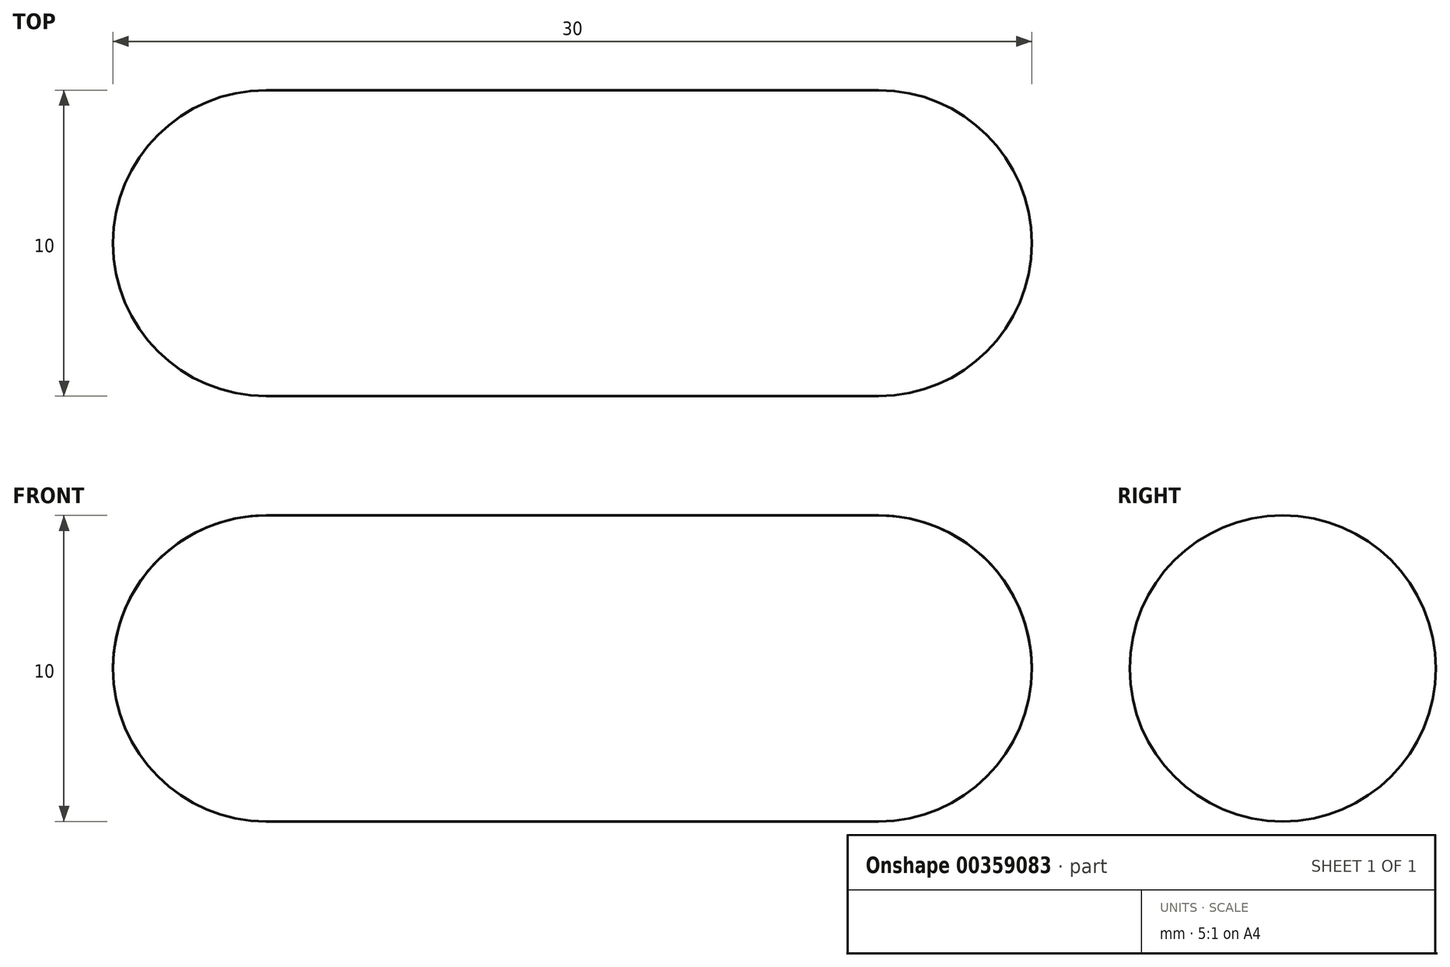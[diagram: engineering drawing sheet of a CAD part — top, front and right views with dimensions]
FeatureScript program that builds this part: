
annotation { "Feature Type Name" : "Feature", "Feature Type Description" : "" }
export const myFeature = defineFeature(function(context is Context, id is Id, definition is map)
    precondition{}
    {
        {
            var Q0;
            Q0=qCreatedBy(makeId("Top.planeOp"),FACE);
            var sketch = newSketch(context, id + "F0", { "sketchPlane" : qUnion([Q0])});
            skLineSegment(sketch, "E0.bottom", {"start": v(0, 0) * mm, "end": v(30, 0) * mm});
            skLineSegment(sketch, "E0.top", {"start": v(0, 10) * mm, "end": v(30, 10) * mm});
            skLineSegment(sketch, "E0.left", {"start": v(0, 0) * mm, "end": v(0, 10) * mm});
            skLineSegment(sketch, "E0.right", {"start": v(30, 0) * mm, "end": v(30, 10) * mm});
            skSolve(sketch);
        }
        {
            var Q0;
            Q0 = qSketchRegion(id + "F0", true);
            extrude(context, id + "F1", {"entities" : qUnion([Q0]), "depth" : 10 * mm});
        }
        {
            var Q0;
            Q0=makeQuery(id+"F1.opExtrude","CAP_EDGE",EDGE,{"disambiguationData":[OSD([sQuery(id+"F0.wireOp",EDGE,"E0.bottom")])],"isStart":false});
            var Q1;
            Q1=makeQuery(id+"F1.opExtrude","CAP_EDGE",EDGE,{"disambiguationData":[OSD([sQuery(id+"F0.wireOp",EDGE,"E0.bottom")])],"isStart":true});
            var Q2;
            Q2=makeQuery(id+"F1.opExtrude","CAP_EDGE",EDGE,{"disambiguationData":[OSD([sQuery(id+"F0.wireOp",EDGE,"E0.top")])],"isStart":true});
            var Q3;
            Q3=makeQuery(id+"F1.opExtrude","CAP_EDGE",EDGE,{"disambiguationData":[OSD([sQuery(id+"F0.wireOp",EDGE,"E0.top")])],"isStart":false});
            fillet(context, id + "F2", {"entities" : qUnion([Q0, Q1, Q2, Q3]), "radius" : 5 * mm, "tangentPropagation" : true, "allowEdgeOverflow" : false});
        }
        {
            var Q0;
            Q0=makeQuery(id+"F1.opExtrude","SWEPT_FACE",FACE,{"disambiguationData":[OSD([sQuery(id+"F0.wireOp",EDGE,"E0.right")])]});
            var Q1;
            Q1=makeQuery(id+"F1.opExtrude","SWEPT_FACE",FACE,{"disambiguationData":[OSD([sQuery(id+"F0.wireOp",EDGE,"E0.left")])]});
            fillet(context, id + "F3", {"entities" : qUnion([Q0, Q1]), "radius" : 5 * mm, "tangentPropagation" : true, "allowEdgeOverflow" : false});
        }
    });
